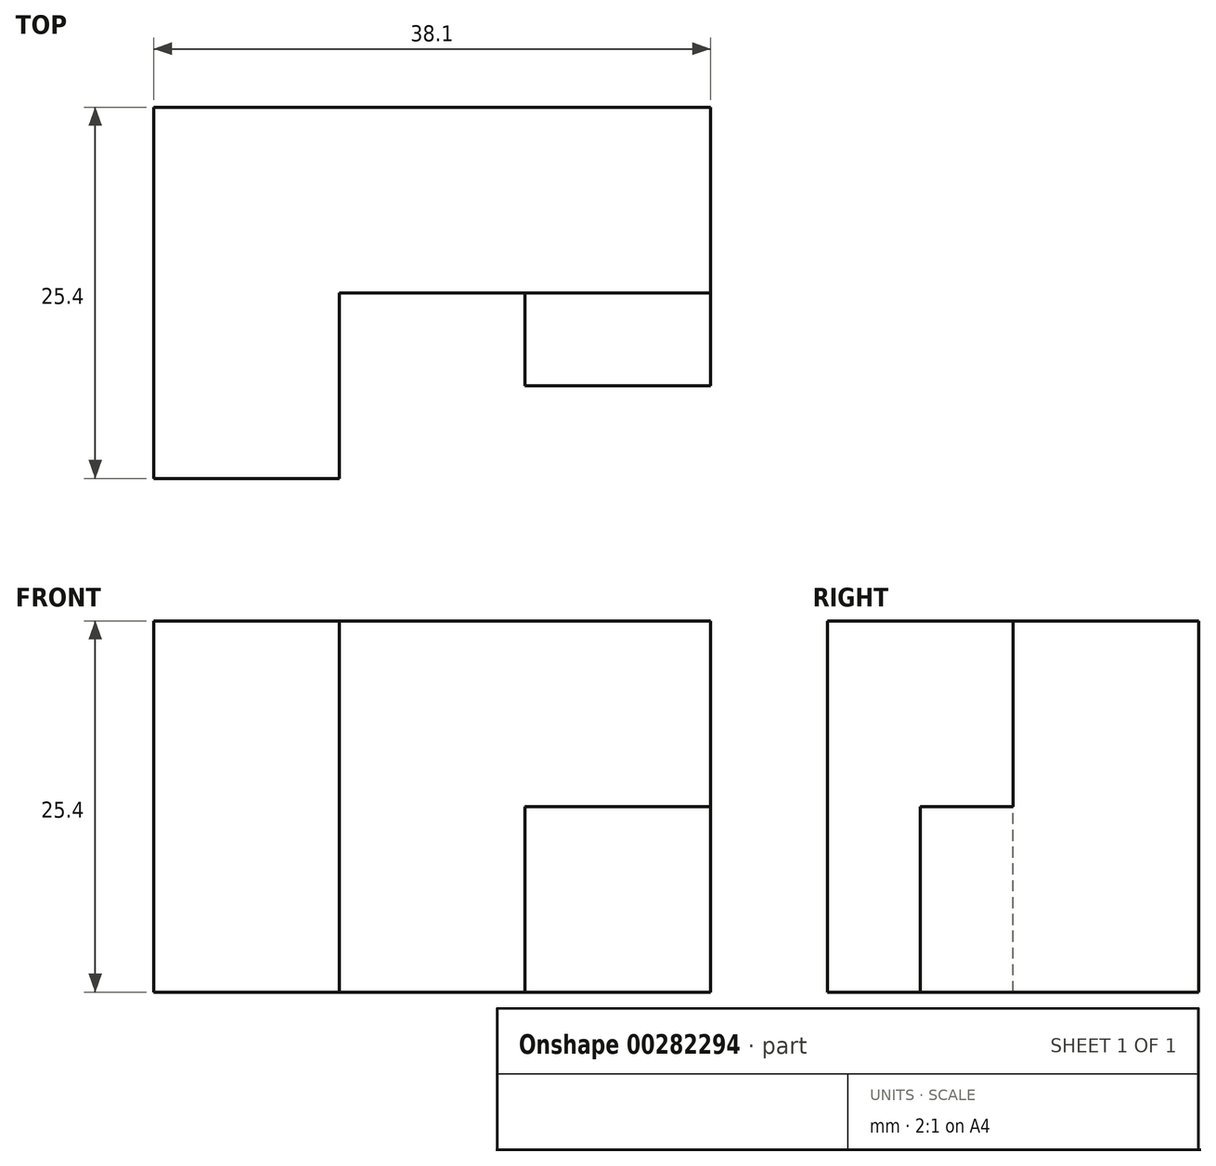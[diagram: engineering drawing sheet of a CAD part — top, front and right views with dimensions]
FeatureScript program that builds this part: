
annotation { "Feature Type Name" : "Feature", "Feature Type Description" : "" }
export const myFeature = defineFeature(function(context is Context, id is Id, definition is map)
    precondition{}
    {
        {
            var Q0;
            Q0=qCreatedBy(makeId("Top.planeOp"),FACE);
            var sketch = newSketch(context, id + "F0", { "sketchPlane" : qUnion([Q0])});
            skLineSegment(sketch, "E0", {"start": v(0, 0) * mm, "end": v(0, 25.4) * mm});
            skLineSegment(sketch, "E1", {"start": v(0, 25.4) * mm, "end": v(38.1, 25.4) * mm});
            skLineSegment(sketch, "E2", {"start": v(38.1, 25.4) * mm, "end": v(38.1, 12.7) * mm});
            skLineSegment(sketch, "E3", {"start": v(38.1, 12.7) * mm, "end": v(12.7, 12.7) * mm});
            skLineSegment(sketch, "E4", {"start": v(12.7, 12.7) * mm, "end": v(12.7, 0) * mm});
            skLineSegment(sketch, "E5", {"start": v(12.7, 0) * mm, "end": v(0, 0) * mm});
            skSolve(sketch);
        }
        {
            var Q0;
            Q0 = qSketchRegion(id + "F0", true);
            extrude(context, id + "F1", {"entities" : qUnion([Q0]), "depth" : 25.4 * mm});
        }
        {
            var Q0;
            Q0=makeQuery(id+"F1.opExtrude","SWEPT_FACE",FACE,{"disambiguationData":[OSD([sQuery(id+"F0.wireOp",EDGE,"E3")])]});
            var sketch = newSketch(context, id + "F2", { "sketchPlane" : qUnion([Q0])});
            skPoint(sketch, "E6.oppositeSnap0", {"position": v(25.4, 25.4) * mm});
            skLineSegment(sketch, "E6.bottom", {"start": v(38.1, 0) * mm, "end": v(25.4, 0) * mm});
            skLineSegment(sketch, "E6.top", {"start": v(38.1, 12.7) * mm, "end": v(25.4, 12.7) * mm});
            skLineSegment(sketch, "E6.left", {"start": v(38.1, 0) * mm, "end": v(38.1, 12.7) * mm});
            skLineSegment(sketch, "E6.right", {"start": v(25.4, 0) * mm, "end": v(25.4, 12.7) * mm});
            skSolve(sketch);
        }
        {
            var Q0;
            Q0 = qSketchRegion(id + "F2", true);
            extrude(context, id + "F3", {"entities" : qUnion([Q0]), "operationType" : NewBodyOperationType.ADD, "depth" : 6.35 * mm});
        }
    });
